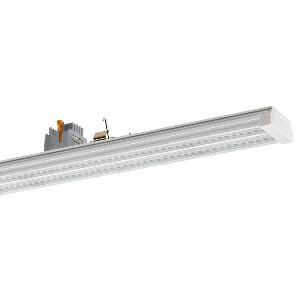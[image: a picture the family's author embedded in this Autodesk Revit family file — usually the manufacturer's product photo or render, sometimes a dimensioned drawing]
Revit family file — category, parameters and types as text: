
# Revit family: conveo_-_cvg_15000_850_w-l_da_7_226848309-00804969_2284
name_source: partatom
category: Lighting Fixtures
units: mm (PartAtom-declared; Revit-internal decimal feet)

## family parameters
Cut with Voids When Loaded = No
Host = Face
Light Source = No
Part Type = Normal
Room Calculation Point = No
Round Connector Dimension = Use Diameter
Shared = No

## types (1)
- CONVEO - CVG 15000/850/W-L/DA/7 (1 x LED, 14800 lm, 5000K)
    Apparent Load = 86 VA
    Approval mark = CE
    CIE Flux Codes = 85 97 99 100 100
    Color Rendering = 80-89
    Color Temperature = 5000K
    Control Gear = Electronic ballast
    Default Elevation = 1800 mm
    Description = CVG 15000/850/W-L/DA/7|Continuous-row system|light source: LED|work equipment: Adjustable electronic ballast, digital DALI|connected load: 220-240 V, 50-60 Hz|Power consumption: approx. 86 W|luminous flux: 14800 lm|luminous efficacy: 172 lm/W|colour temperature: Cold white, ca. 5000 K|color rendering index (CRI): >= 80|chromaticity tolerance:  3 SDCM|System of protection: IP 54|class of protection: I|technology: Continuously dimmable|luminaire body|material: Aluminium|surface: Powder coatet|colour: White|lamp cover: Acrylic (PMMA), Satine|weight (net): approx. 2.2 kg|Fastening: Available separately|maximum ambient temperature: 41 ░C|glare control: Lens optics|Approval mark: VDE - ENEC|
    Frequency = 50 Hz
    Height = 70 mm
    Lamp = 1 x LED
    Lamp Light Flux = 14800 lm
    Lamp count = 1
    Length = 1500 mm
    Luminous efficacy = 172 lm/W
    Manufacturer = Waldmann
    ModVariant = No
    Model = 226848309-00804969
    Mounting Place = Ceiling
    Mounting Type = Pendant
    Number of Poles = 1
    OnlyDefault = Yes
    Power Factor = 1
    Product Name = CONVEO - CVG 15000/850/W-L/DA/7
    Product group = Continuous-row system (industry)
    ProductGroupID = 301
    Protection Class = Protection class I
    Protection Degree = IP 54
    RLX_Detail_Level = 1
    RlxData = <blob elided: 136097 chars, md5=3c5c0269>
    Socket = socket
    Standby Power = 0 W
    System Light Flux = 14800 lm
    System Power = 86 W
    Type Comments = Product without accessories
    Type Image = 226848299-00804968_2l7.jpg
    URL = http://relux.com
    VarID = ---
    Voltage = 230 V
    Voltage Range = 220-240 V
    Weight = 0.00 kg
    Width = 64 mm

## geometry (parser evidence)
native form markers: Blend x4, Sweep x9
no freeform markers — native parametric forms only
